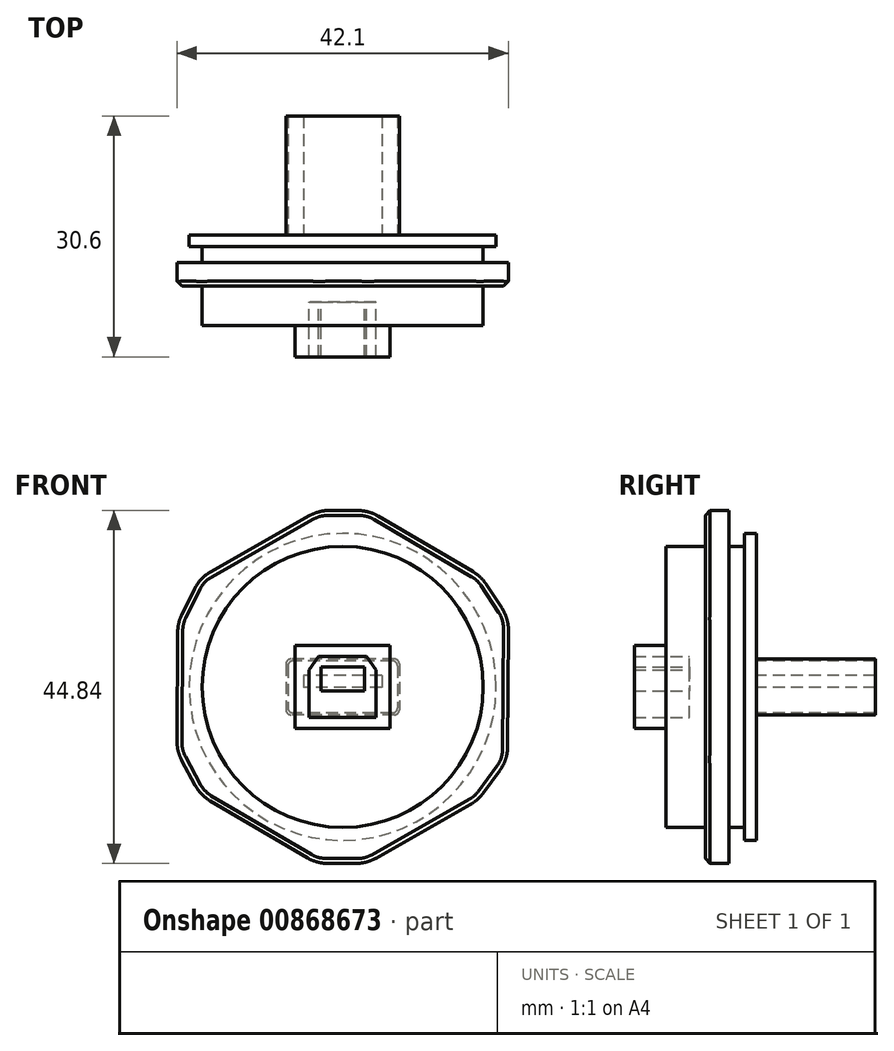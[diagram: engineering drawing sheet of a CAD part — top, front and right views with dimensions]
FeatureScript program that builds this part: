
annotation { "Feature Type Name" : "Feature", "Feature Type Description" : "" }
export const myFeature = defineFeature(function(context is Context, id is Id, definition is map)
    precondition{}
    {
        {
            var Q0;
            Q0=qCreatedBy(makeId("Front.planeOp"),FACE);
            var sketch = newSketch(context, id + "F0", { "sketchPlane" : qUnion([Q0])});
            skCircle(sketch, "E0", {"center": v(0, 0) * mm, "radius": 17.85 * mm});
            skSolve(sketch);
        }
        {
            var Q0;
            Q0 = qSketchRegion(id + "F0", true);
            extrude(context, id + "F1", {"entities" : qUnion([Q0]), "endBound" : BoundingType.SYMMETRIC, "depth" : 10 * mm, "offsetDistance" : 25.4 * mm});
        }
        {
            var Q0;
            Q0=makeQuery(id+"F1.opExtrude","CAP_FACE",FACE,{"disambiguationData":[OSD([sQuery(id+"F0.wireOp",EDGE,"E0")])],"isStart":true});
            cPlane(context, id + "F2", {"entities" : qUnion([Q0]), "cplaneType" : CPlaneType.OFFSET, "offset" : 2 * mm, "oppositeDirection" : true, "width" : 152.4 * mm, "height" : 152.4 * mm});
        }
        {
            var Q0;
            Q0=qCreatedBy(id+"F2.planeOp",FACE);
            var sketch = newSketch(context, id + "F3", { "sketchPlane" : qUnion([Q0])});
            skCircle(sketch, "E1.cCircle", {"center": v(0, 0) * mm, "radius": 21 * mm, "construction": true});
            skLineSegment(sketch, "E1.0", {"start": v(-17.56, 14.05) * mm, "end": v(-3.3, 22.42) * mm});
            skLineSegment(sketch, "E1.1", {"start": v(3.06, 22.42) * mm, "end": v(18.13, 13.85) * mm});
            skLineSegment(sketch, "E1.2", {"start": v(20.94, 8.15) * mm, "end": v(21.06, -8.17) * mm});
            skLineSegment(sketch, "E1.3", {"start": v(18.05, -13.76) * mm, "end": v(3.3, -22.42) * mm});
            skLineSegment(sketch, "E1.4", {"start": v(-3.06, -22.42) * mm, "end": v(-17.16, -14.4) * mm});
            skLineSegment(sketch, "E1.5", {"start": v(-20.94, -9.3) * mm, "end": v(-21.06, 8.75) * mm});
            skPoint(sketch, "E1.0.midPoint", {"position": v(-10.62, 18.11) * mm});
            skLineSegment(sketch, "E2", {"start": v(-21.06, 8.75) * mm, "end": v(-17.56, 14.05) * mm});
            skLineSegment(sketch, "E3", {"start": v(-3.3, 22.42) * mm, "end": v(3.06, 22.42) * mm});
            skLineSegment(sketch, "E4", {"start": v(18.13, 13.85) * mm, "end": v(20.94, 8.15) * mm});
            skLineSegment(sketch, "E5", {"start": v(21.06, -8.17) * mm, "end": v(18.05, -13.76) * mm});
            skLineSegment(sketch, "E6", {"start": v(3.3, -22.42) * mm, "end": v(-3.06, -22.42) * mm});
            skLineSegment(sketch, "E7", {"start": v(-17.16, -14.4) * mm, "end": v(-20.94, -9.3) * mm});
            skPoint(sketch, "E8.orphan", {"position": v(-21.08, 11.98) * mm});
            skPoint(sketch, "E9.orphan", {"position": v(-0.17, 24.25) * mm});
            skPoint(sketch, "E10.orphan", {"position": v(20.92, 12.27) * mm});
            skPoint(sketch, "E11.orphan", {"position": v(21.08, -11.98) * mm});
            skPoint(sketch, "E12.orphan", {"position": v(0.17, -24.25) * mm});
            skPoint(sketch, "E13.orphan", {"position": v(-20.92, -12.27) * mm});
            skSolve(sketch);
        }
        {
            var Q0;
            Q0 = qSketchRegion(id + "F3", true);
            extrude(context, id + "F4", {"entities" : qUnion([Q0]), "operationType" : NewBodyOperationType.ADD, "oppositeDirection" : true, "depth" : 3 * mm, "offsetDistance" : 25.4 * mm});
        }
        {
            var Q0;
            Q0=makeQuery(id+"F4.opExtrude","CAP_EDGE",EDGE,{"disambiguationData":[OSD([sQuery(id+"F3.wireOp",EDGE,"E1.0")])],"isStart":false});
            var Q1;
            Q1=makeQuery(id+"F4.opExtrude","CAP_EDGE",EDGE,{"disambiguationData":[OSD([sQuery(id+"F3.wireOp",EDGE,"E2")])],"isStart":false});
            var Q2;
            Q2=makeQuery(id+"F4.opExtrude","CAP_EDGE",EDGE,{"disambiguationData":[OSD([sQuery(id+"F3.wireOp",EDGE,"E1.5")])],"isStart":false});
            var Q3;
            Q3=makeQuery(id+"F4.opExtrude","CAP_EDGE",EDGE,{"disambiguationData":[OSD([sQuery(id+"F3.wireOp",EDGE,"E7")])],"isStart":false});
            var Q4;
            Q4=makeQuery(id+"F4.opExtrude","CAP_EDGE",EDGE,{"disambiguationData":[OSD([sQuery(id+"F3.wireOp",EDGE,"E1.4")])],"isStart":false});
            var Q5;
            Q5=makeQuery(id+"F4.opExtrude","CAP_EDGE",EDGE,{"disambiguationData":[OSD([sQuery(id+"F3.wireOp",EDGE,"E6")])],"isStart":false});
            var Q6;
            Q6=makeQuery(id+"F4.opExtrude","CAP_EDGE",EDGE,{"disambiguationData":[OSD([sQuery(id+"F3.wireOp",EDGE,"E1.3")])],"isStart":false});
            var Q7;
            Q7=makeQuery(id+"F4.opExtrude","CAP_EDGE",EDGE,{"disambiguationData":[OSD([sQuery(id+"F3.wireOp",EDGE,"E5")])],"isStart":false});
            var Q8;
            Q8=makeQuery(id+"F4.opExtrude","CAP_EDGE",EDGE,{"disambiguationData":[OSD([sQuery(id+"F3.wireOp",EDGE,"E1.2")])],"isStart":false});
            var Q9;
            Q9=makeQuery(id+"F4.opExtrude","CAP_EDGE",EDGE,{"disambiguationData":[OSD([sQuery(id+"F3.wireOp",EDGE,"E4")])],"isStart":false});
            var Q10;
            Q10=makeQuery(id+"F4.opExtrude","CAP_EDGE",EDGE,{"disambiguationData":[OSD([sQuery(id+"F3.wireOp",EDGE,"E1.1")])],"isStart":false});
            var Q11;
            Q11=makeQuery(id+"F4.opExtrude","CAP_EDGE",EDGE,{"disambiguationData":[OSD([sQuery(id+"F3.wireOp",EDGE,"E3")])],"isStart":false});
            chamfer(context, id + "F5", {"entities" : qUnion([Q0, Q1, Q2, Q3, Q4, Q5, Q6, Q7, Q8, Q9, Q10, Q11]), "width" : 0.64 * mm, "tangentPropagation" : true});
        }
        {
            var Q0;
            Q0=makeQuery(id+"F4.opExtrude","SWEPT_EDGE",EDGE,{"disambiguationData":[OSD([sQuery(id+"F3.wireOp",EDGE,"E1.0"),sQuery(id+"F3.wireOp",EDGE,"E2")])]});
            var Q1;
            Q1=makeQuery(id+"F5.opChamfer","BLEND_EDGE",EDGE,{"blendedFrom":[makeQuery(id+"F4.opExtrude","CAP_EDGE",EDGE,{"disambiguationData":[OSD([sQuery(id+"F3.wireOp",EDGE,"E1.0")])],"isStart":false}),makeQuery(id+"F4.opExtrude","CAP_EDGE",EDGE,{"disambiguationData":[OSD([sQuery(id+"F3.wireOp",EDGE,"E2")])],"isStart":false})],"blendedInto":[]});
            var Q2;
            Q2=makeQuery(id+"F5.opChamfer","BLEND_EDGE",EDGE,{"blendedFrom":[makeQuery(id+"F4.opExtrude","CAP_EDGE",EDGE,{"disambiguationData":[OSD([sQuery(id+"F3.wireOp",EDGE,"E1.5")])],"isStart":false}),makeQuery(id+"F4.opExtrude","CAP_EDGE",EDGE,{"disambiguationData":[OSD([sQuery(id+"F3.wireOp",EDGE,"E2")])],"isStart":false})],"blendedInto":[]});
            var Q3;
            Q3=makeQuery(id+"F4.opExtrude","SWEPT_EDGE",EDGE,{"disambiguationData":[OSD([sQuery(id+"F3.wireOp",EDGE,"E1.5"),sQuery(id+"F3.wireOp",EDGE,"E2")])]});
            var Q4;
            Q4=makeQuery(id+"F5.opChamfer","BLEND_EDGE",EDGE,{"blendedFrom":[makeQuery(id+"F4.opExtrude","CAP_EDGE",EDGE,{"disambiguationData":[OSD([sQuery(id+"F3.wireOp",EDGE,"E1.5")])],"isStart":false}),makeQuery(id+"F4.opExtrude","CAP_EDGE",EDGE,{"disambiguationData":[OSD([sQuery(id+"F3.wireOp",EDGE,"E7")])],"isStart":false})],"blendedInto":[]});
            var Q5;
            Q5=makeQuery(id+"F4.opExtrude","SWEPT_EDGE",EDGE,{"disambiguationData":[OSD([sQuery(id+"F3.wireOp",EDGE,"E1.5"),sQuery(id+"F3.wireOp",EDGE,"E7")])]});
            var Q6;
            Q6=makeQuery(id+"F5.opChamfer","BLEND_EDGE",EDGE,{"blendedFrom":[makeQuery(id+"F4.opExtrude","CAP_EDGE",EDGE,{"disambiguationData":[OSD([sQuery(id+"F3.wireOp",EDGE,"E1.4")])],"isStart":false}),makeQuery(id+"F4.opExtrude","CAP_EDGE",EDGE,{"disambiguationData":[OSD([sQuery(id+"F3.wireOp",EDGE,"E7")])],"isStart":false})],"blendedInto":[]});
            var Q7;
            Q7=makeQuery(id+"F4.opExtrude","SWEPT_EDGE",EDGE,{"disambiguationData":[OSD([sQuery(id+"F3.wireOp",EDGE,"E1.4"),sQuery(id+"F3.wireOp",EDGE,"E7")])]});
            var Q8;
            Q8=makeQuery(id+"F5.opChamfer","BLEND_EDGE",EDGE,{"blendedFrom":[makeQuery(id+"F4.opExtrude","CAP_EDGE",EDGE,{"disambiguationData":[OSD([sQuery(id+"F3.wireOp",EDGE,"E1.4")])],"isStart":false}),makeQuery(id+"F4.opExtrude","CAP_EDGE",EDGE,{"disambiguationData":[OSD([sQuery(id+"F3.wireOp",EDGE,"E6")])],"isStart":false})],"blendedInto":[]});
            var Q9;
            Q9=makeQuery(id+"F4.opExtrude","SWEPT_EDGE",EDGE,{"disambiguationData":[OSD([sQuery(id+"F3.wireOp",EDGE,"E1.4"),sQuery(id+"F3.wireOp",EDGE,"E6")])]});
            var Q10;
            Q10=makeQuery(id+"F5.opChamfer","BLEND_EDGE",EDGE,{"blendedFrom":[makeQuery(id+"F4.opExtrude","CAP_EDGE",EDGE,{"disambiguationData":[OSD([sQuery(id+"F3.wireOp",EDGE,"E1.3")])],"isStart":false}),makeQuery(id+"F4.opExtrude","CAP_EDGE",EDGE,{"disambiguationData":[OSD([sQuery(id+"F3.wireOp",EDGE,"E6")])],"isStart":false})],"blendedInto":[]});
            var Q11;
            Q11=makeQuery(id+"F4.opExtrude","SWEPT_EDGE",EDGE,{"disambiguationData":[OSD([sQuery(id+"F3.wireOp",EDGE,"E1.3"),sQuery(id+"F3.wireOp",EDGE,"E6")])]});
            var Q12;
            Q12=makeQuery(id+"F5.opChamfer","BLEND_EDGE",EDGE,{"blendedFrom":[makeQuery(id+"F4.opExtrude","CAP_EDGE",EDGE,{"disambiguationData":[OSD([sQuery(id+"F3.wireOp",EDGE,"E1.3")])],"isStart":false}),makeQuery(id+"F4.opExtrude","CAP_EDGE",EDGE,{"disambiguationData":[OSD([sQuery(id+"F3.wireOp",EDGE,"E5")])],"isStart":false})],"blendedInto":[]});
            var Q13;
            Q13=makeQuery(id+"F4.opExtrude","SWEPT_EDGE",EDGE,{"disambiguationData":[OSD([sQuery(id+"F3.wireOp",EDGE,"E1.3"),sQuery(id+"F3.wireOp",EDGE,"E5")])]});
            var Q14;
            Q14=makeQuery(id+"F4.opExtrude","SWEPT_EDGE",EDGE,{"disambiguationData":[OSD([sQuery(id+"F3.wireOp",EDGE,"E1.2"),sQuery(id+"F3.wireOp",EDGE,"E5")])]});
            var Q15;
            Q15=makeQuery(id+"F5.opChamfer","BLEND_EDGE",EDGE,{"blendedFrom":[makeQuery(id+"F4.opExtrude","CAP_EDGE",EDGE,{"disambiguationData":[OSD([sQuery(id+"F3.wireOp",EDGE,"E1.2")])],"isStart":false}),makeQuery(id+"F4.opExtrude","CAP_EDGE",EDGE,{"disambiguationData":[OSD([sQuery(id+"F3.wireOp",EDGE,"E5")])],"isStart":false})],"blendedInto":[]});
            var Q16;
            Q16=makeQuery(id+"F4.opExtrude","SWEPT_EDGE",EDGE,{"disambiguationData":[OSD([sQuery(id+"F3.wireOp",EDGE,"E1.2"),sQuery(id+"F3.wireOp",EDGE,"E4")])]});
            var Q17;
            Q17=makeQuery(id+"F5.opChamfer","BLEND_EDGE",EDGE,{"blendedFrom":[makeQuery(id+"F4.opExtrude","CAP_EDGE",EDGE,{"disambiguationData":[OSD([sQuery(id+"F3.wireOp",EDGE,"E1.2")])],"isStart":false}),makeQuery(id+"F4.opExtrude","CAP_EDGE",EDGE,{"disambiguationData":[OSD([sQuery(id+"F3.wireOp",EDGE,"E4")])],"isStart":false})],"blendedInto":[]});
            var Q18;
            Q18=makeQuery(id+"F4.opExtrude","SWEPT_EDGE",EDGE,{"disambiguationData":[OSD([sQuery(id+"F3.wireOp",EDGE,"E1.1"),sQuery(id+"F3.wireOp",EDGE,"E4")])]});
            var Q19;
            Q19=makeQuery(id+"F5.opChamfer","BLEND_EDGE",EDGE,{"blendedFrom":[makeQuery(id+"F4.opExtrude","CAP_EDGE",EDGE,{"disambiguationData":[OSD([sQuery(id+"F3.wireOp",EDGE,"E1.1")])],"isStart":false}),makeQuery(id+"F4.opExtrude","CAP_EDGE",EDGE,{"disambiguationData":[OSD([sQuery(id+"F3.wireOp",EDGE,"E4")])],"isStart":false})],"blendedInto":[]});
            var Q20;
            Q20=makeQuery(id+"F4.opExtrude","SWEPT_EDGE",EDGE,{"disambiguationData":[OSD([sQuery(id+"F3.wireOp",EDGE,"E1.1"),sQuery(id+"F3.wireOp",EDGE,"E3")])]});
            var Q21;
            Q21=makeQuery(id+"F5.opChamfer","BLEND_EDGE",EDGE,{"blendedFrom":[makeQuery(id+"F4.opExtrude","CAP_EDGE",EDGE,{"disambiguationData":[OSD([sQuery(id+"F3.wireOp",EDGE,"E1.1")])],"isStart":false}),makeQuery(id+"F4.opExtrude","CAP_EDGE",EDGE,{"disambiguationData":[OSD([sQuery(id+"F3.wireOp",EDGE,"E3")])],"isStart":false})],"blendedInto":[]});
            var Q22;
            Q22=makeQuery(id+"F4.opExtrude","SWEPT_EDGE",EDGE,{"disambiguationData":[OSD([sQuery(id+"F3.wireOp",EDGE,"E1.0"),sQuery(id+"F3.wireOp",EDGE,"E3")])]});
            var Q23;
            Q23=makeQuery(id+"F5.opChamfer","BLEND_EDGE",EDGE,{"blendedFrom":[makeQuery(id+"F4.opExtrude","CAP_EDGE",EDGE,{"disambiguationData":[OSD([sQuery(id+"F3.wireOp",EDGE,"E1.0")])],"isStart":false}),makeQuery(id+"F4.opExtrude","CAP_EDGE",EDGE,{"disambiguationData":[OSD([sQuery(id+"F3.wireOp",EDGE,"E3")])],"isStart":false})],"blendedInto":[]});
            fillet(context, id + "F6", {"entities" : qUnion([Q0, Q1, Q2, Q3, Q4, Q5, Q6, Q7, Q8, Q9, Q10, Q11, Q12, Q13, Q14, Q15, Q16, Q17, Q18, Q19, Q20, Q21, Q22, Q23]), "radius" : 5.08 * mm, "tangentPropagation" : true, "allowEdgeOverflow" : false});
        }
        {
            var Q0;
            Q0=makeQuery(id+"F1.opExtrude","CAP_FACE",FACE,{"disambiguationData":[OSD([sQuery(id+"F0.wireOp",EDGE,"E0")])],"isStart":true});
            var sketch = newSketch(context, id + "F7", { "sketchPlane" : qUnion([Q0])});
            skCircle(sketch, "E14", {"center": v(0, 0) * mm, "radius": 19.5 * mm});
            skSolve(sketch);
        }
        {
            var Q0;
            Q0 = qSketchRegion(id + "F7", true);
            extrude(context, id + "F8", {"entities" : qUnion([Q0]), "operationType" : NewBodyOperationType.ADD, "depth" : 1.5 * mm, "offsetDistance" : 25.4 * mm});
        }
        {
            var Q0;
            Q0=makeQuery(id+"F1.opExtrude","CAP_FACE",FACE,{"disambiguationData":[OSD([sQuery(id+"F0.wireOp",EDGE,"E0")])],"isStart":false});
            var sketch = newSketch(context, id + "F9", { "sketchPlane" : qUnion([Q0])});
            skLineSegment(sketch, "E15.bottom", {"start": v(-6.02, 5.3) * mm, "end": v(6.02, 5.3) * mm});
            skLineSegment(sketch, "E15.top", {"start": v(-6.02, -5.3) * mm, "end": v(6.02, -5.3) * mm});
            skLineSegment(sketch, "E15.left", {"start": v(-6.02, 5.3) * mm, "end": v(-6.02, -5.3) * mm});
            skLineSegment(sketch, "E15.right", {"start": v(6.02, 5.3) * mm, "end": v(6.02, -5.3) * mm});
            skPoint(sketch, "E15.middle", {"position": v(0, 0) * mm});
            skLineSegment(sketch, "E16.bottom", {"start": v(-2.75, 2.52) * mm, "end": v(2.75, 2.52) * mm});
            skLineSegment(sketch, "E16.top", {"start": v(-2.75, -0.53) * mm, "end": v(2.75, -0.53) * mm});
            skLineSegment(sketch, "E16.left", {"start": v(-2.75, 2.52) * mm, "end": v(-2.75, -0.53) * mm});
            skLineSegment(sketch, "E16.right", {"start": v(2.75, 2.52) * mm, "end": v(2.75, -0.53) * mm});
            skPoint(sketch, "E16.middle", {"position": v(0, 1) * mm});
            skLineSegment(sketch, "E17", {"start": v(-4.26, -3.9) * mm, "end": v(-4.26, 2.15) * mm});
            skLineSegment(sketch, "E18", {"start": v(-4.26, 2.15) * mm, "end": v(-3.05, 3.88) * mm});
            skLineSegment(sketch, "E19", {"start": v(-3.05, 3.88) * mm, "end": v(3.03, 3.88) * mm});
            skLineSegment(sketch, "E20", {"start": v(3.03, 3.88) * mm, "end": v(4.24, 2.15) * mm});
            skLineSegment(sketch, "E21", {"start": v(4.24, 2.15) * mm, "end": v(4.24, -3.9) * mm});
            skLineSegment(sketch, "E22", {"start": v(4.24, -3.9) * mm, "end": v(-4.26, -3.9) * mm});
            skSolve(sketch);
        }
        {
            var Q0;
            Q0=makeQuery(id+"F9.imprint","IMPRINT",FACE,{"disambiguationData":[TD([[makeQuery(id+"F9.imprint","IMPRINT",EDGE,{"derivedFrom":sQuery(id+"F9.wireOp",EDGE,"E15.bottom")}),-1.0]])]});
            var Q1;
            Q1=makeQuery(id+"F9.imprint","IMPRINT",FACE,{"disambiguationData":[TD([[makeQuery(id+"F9.imprint","IMPRINT",EDGE,{"derivedFrom":sQuery(id+"F9.wireOp",EDGE,"E16.bottom")}),-1.0]])]});
            extrude(context, id + "F10", {"entities" : qUnion([Q0, Q1]), "operationType" : NewBodyOperationType.ADD, "depth" : 4 * mm, "offsetDistance" : 25.4 * mm});
        }
        {
            var Q0;
            Q0=makeQuery(id+"F9.imprint","IMPRINT",FACE,{"disambiguationData":[TD([[makeQuery(id+"F9.imprint","IMPRINT",EDGE,{"derivedFrom":sQuery(id+"F9.wireOp",EDGE,"E16.bottom")}),1.0]])]});
            extrude(context, id + "F11", {"entities" : qUnion([Q0]), "operationType" : NewBodyOperationType.REMOVE, "oppositeDirection" : true, "depth" : 3 * mm, "offsetDistance" : 25.4 * mm});
        }
        {
            var Q0;
            Q0=makeQuery(id+"F8.opExtrude","CAP_FACE",FACE,{"disambiguationData":[OSD([sQuery(id+"F7.wireOp",EDGE,"E14")])],"isStart":false});
            var sketch = newSketch(context, id + "F12", { "sketchPlane" : qUnion([Q0])});
            skLineSegment(sketch, "E23.bottom", {"start": v(-6.56, 3.55) * mm, "end": v(6.57, 3.55) * mm});
            skLineSegment(sketch, "E23.top", {"start": v(-6.57, -3.55) * mm, "end": v(6.57, -3.55) * mm});
            skLineSegment(sketch, "E23.left", {"start": v(-7.2, 2.91) * mm, "end": v(-7.2, -2.91) * mm});
            skLineSegment(sketch, "E23.right", {"start": v(7.2, 2.92) * mm, "end": v(7.2, -2.91) * mm});
            skPoint(sketch, "E23.middle", {"position": v(0, 0) * mm});
            skLineSegment(sketch, "E24.bottom", {"start": v(-5, 1.45) * mm, "end": v(5, 1.45) * mm});
            skLineSegment(sketch, "E24.top", {"start": v(-5, -0.05) * mm, "end": v(5, -0.05) * mm});
            skLineSegment(sketch, "E24.left", {"start": v(-5, 1.45) * mm, "end": v(-5, -0.05) * mm});
            skLineSegment(sketch, "E24.right", {"start": v(5, 1.45) * mm, "end": v(5, -0.05) * mm});
            skPoint(sketch, "E24.middle", {"position": v(0, 0.7) * mm});
            skPoint(sketch, "E25.visualSharp", {"position": v(-7.2, 3.55) * mm});
            skArc(sketch, "E25.filletArc", {"start": v(-6.56, 3.55) * mm, "mid": v(-7.01, 3.36) * mm, "end": v(-7.2, 2.91) * mm});
            skPoint(sketch, "E26.visualSharp", {"position": v(-7.2, -3.55) * mm});
            skArc(sketch, "E26.filletArc", {"start": v(-7.2, -2.91) * mm, "mid": v(-7.01, -3.36) * mm, "end": v(-6.57, -3.55) * mm});
            skPoint(sketch, "E27.visualSharp", {"position": v(7.2, -3.55) * mm});
            skArc(sketch, "E27.filletArc", {"start": v(6.57, -3.55) * mm, "mid": v(7.01, -3.36) * mm, "end": v(7.2, -2.91) * mm});
            skPoint(sketch, "E28.visualSharp", {"position": v(7.2, 3.55) * mm});
            skArc(sketch, "E28.filletArc", {"start": v(7.2, 2.92) * mm, "mid": v(7.01, 3.36) * mm, "end": v(6.57, 3.55) * mm});
            skLineSegment(sketch, "E29.bottom", {"start": v(-6.32, 3.3) * mm, "end": v(6.32, 3.3) * mm});
            skLineSegment(sketch, "E29.top", {"start": v(-6.32, -3.3) * mm, "end": v(6.32, -3.3) * mm});
            skLineSegment(sketch, "E29.left", {"start": v(-6.95, 2.67) * mm, "end": v(-6.95, -2.66) * mm});
            skLineSegment(sketch, "E29.right", {"start": v(6.95, 2.67) * mm, "end": v(6.95, -2.66) * mm});
            skPoint(sketch, "E30.visualSharp", {"position": v(-6.95, 3.3) * mm});
            skArc(sketch, "E30.filletArc", {"start": v(-6.32, 3.3) * mm, "mid": v(-6.76, 3.11) * mm, "end": v(-6.95, 2.67) * mm});
            skPoint(sketch, "E31.visualSharp", {"position": v(6.95, 3.3) * mm});
            skArc(sketch, "E31.filletArc", {"start": v(6.95, 2.67) * mm, "mid": v(6.76, 3.11) * mm, "end": v(6.32, 3.3) * mm});
            skPoint(sketch, "E32.visualSharp", {"position": v(6.95, -3.3) * mm});
            skArc(sketch, "E32.filletArc", {"start": v(6.32, -3.3) * mm, "mid": v(6.76, -3.11) * mm, "end": v(6.95, -2.66) * mm});
            skPoint(sketch, "E33.visualSharp", {"position": v(-6.95, -3.3) * mm});
            skArc(sketch, "E33.filletArc", {"start": v(-6.95, -2.66) * mm, "mid": v(-6.76, -3.11) * mm, "end": v(-6.32, -3.3) * mm});
            skSolve(sketch);
        }
        {
            var Q0;
            Q0=makeQuery(id+"F12.imprint","IMPRINT",FACE,{"disambiguationData":[TD([[makeQuery(id+"F12.imprint","IMPRINT",EDGE,{"derivedFrom":sQuery(id+"F12.wireOp",EDGE,"E23.bottom")}),-1.0]])]});
            var Q1;
            Q1=makeQuery(id+"F12.imprint","IMPRINT",FACE,{"disambiguationData":[TD([[makeQuery(id+"F12.imprint","IMPRINT",EDGE,{"derivedFrom":sQuery(id+"F12.wireOp",EDGE,"E24.bottom")}),-1.0]])]});
            extrude(context, id + "F13", {"entities" : qUnion([Q0, Q1]), "operationType" : NewBodyOperationType.ADD, "depth" : 15.1 * mm, "offsetDistance" : 25.4 * mm});
        }
    });
